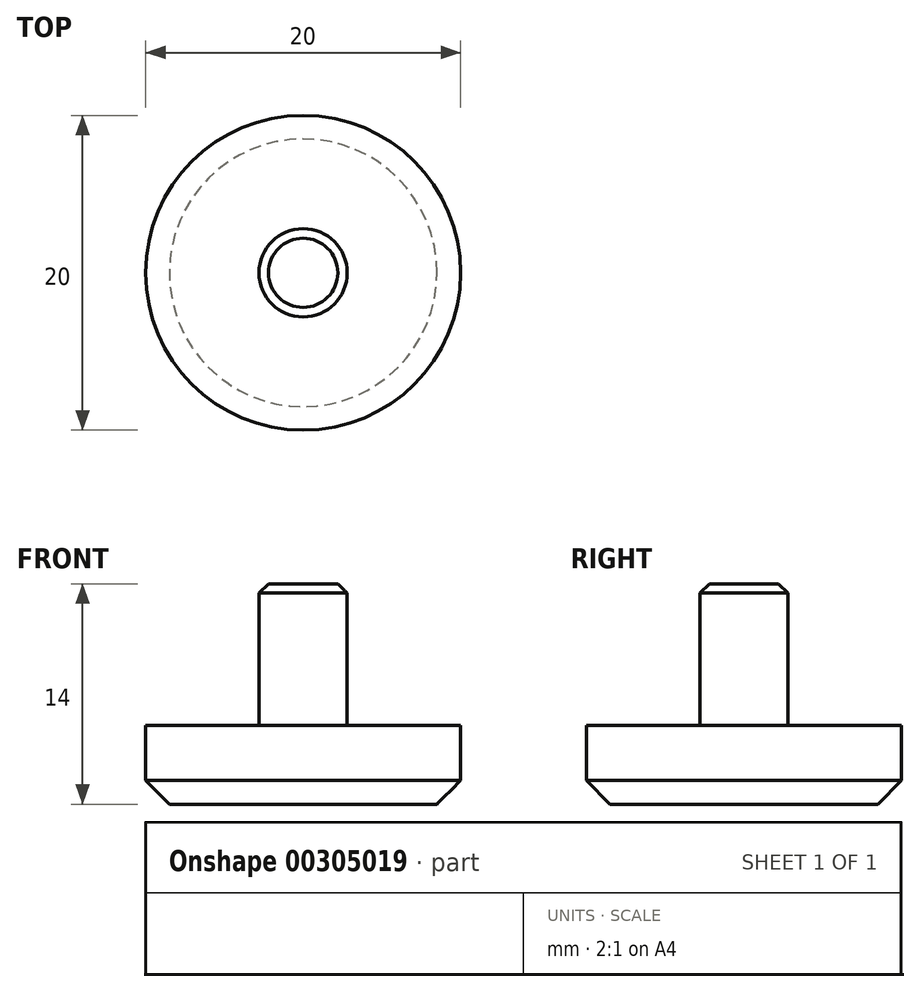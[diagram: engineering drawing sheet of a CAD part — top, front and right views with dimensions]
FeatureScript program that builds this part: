
annotation { "Feature Type Name" : "Feature", "Feature Type Description" : "" }
export const myFeature = defineFeature(function(context is Context, id is Id, definition is map)
    precondition{}
    {
        {
            var Q0;
            Q0=qCreatedBy(makeId("Top.planeOp"),FACE);
            var sketch = newSketch(context, id + "F0", { "sketchPlane" : qUnion([Q0])});
            skCircle(sketch, "E0", {"center": v(0, 0) * mm, "radius": 10 * mm});
            skSolve(sketch);
        }
        {
            var Q0;
            Q0=makeQuery(id+"F0.imprint","IMPRINT",FACE,{"disambiguationData":[TD([[makeQuery(id+"F0.imprint","IMPRINT",EDGE,{"derivedFrom":sQuery(id+"F0.wireOp",EDGE,"E0")}),1.0]])]});
            extrude(context, id + "F1", {"entities" : qUnion([Q0]), "depth" : 5 * mm});
        }
        {
            var Q0;
            Q0=makeQuery(id+"F1.opExtrude","CAP_FACE",FACE,{"disambiguationData":[OSD([sQuery(id+"F0.wireOp",EDGE,"E0")])],"isStart":false});
            var sketch = newSketch(context, id + "F2", { "sketchPlane" : qUnion([Q0])});
            skCircle(sketch, "E1", {"center": v(0, 0) * mm, "radius": 2.8 * mm});
            skSolve(sketch);
        }
        {
            var Q0;
            Q0=makeQuery(id+"F2.imprint","IMPRINT",FACE,{"disambiguationData":[TD([[makeQuery(id+"F2.imprint","IMPRINT",EDGE,{"derivedFrom":sQuery(id+"F2.wireOp",EDGE,"E1")}),1.0]])]});
            extrude(context, id + "F3", {"entities" : qUnion([Q0]), "operationType" : NewBodyOperationType.ADD, "depth" : 9 * mm});
        }
        {
            var Q0;
            Q0=makeQuery(id+"F1.opExtrude","CAP_EDGE",EDGE,{"disambiguationData":[OSD([sQuery(id+"F0.wireOp",EDGE,"E0")])],"isStart":true});
            chamfer(context, id + "F4", {"entities" : qUnion([Q0]), "width" : 1.5 * mm, "tangentPropagation" : true});
        }
        {
            var Q0;
            Q0=makeQuery(id+"F3.opExtrude","CAP_EDGE",EDGE,{"disambiguationData":[OSD([sQuery(id+"F2.wireOp",EDGE,"E1")])],"isStart":false});
            chamfer(context, id + "F5", {"entities" : qUnion([Q0]), "width" : 0.6 * mm, "tangentPropagation" : true});
        }
    });
